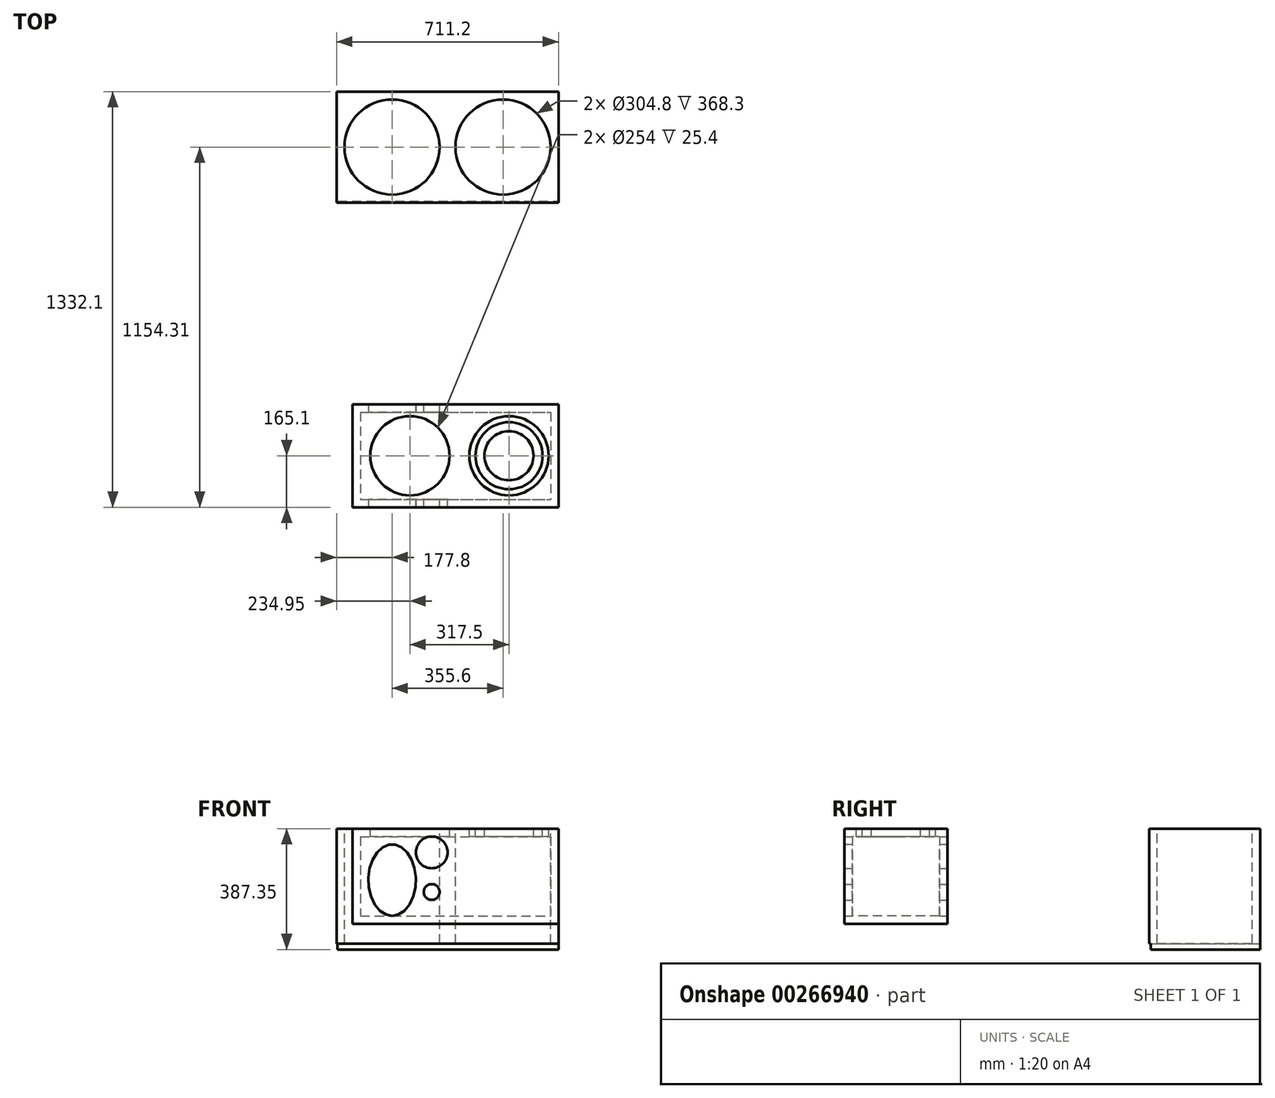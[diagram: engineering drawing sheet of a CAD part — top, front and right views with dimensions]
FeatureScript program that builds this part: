
annotation { "Feature Type Name" : "Feature", "Feature Type Description" : "" }
export const myFeature = defineFeature(function(context is Context, id is Id, definition is map)
    precondition{}
    {
        {
            var Q0;
            Q0=qCreatedBy(makeId("Front.planeOp"),FACE);
            var sketch = newSketch(context, id + "F0", { "sketchPlane" : qUnion([Q0])});
            skLineSegment(sketch, "E0.bottom", {"start": v(-152.4, 304.8) * mm, "end": v(152.4, 304.8) * mm});
            skLineSegment(sketch, "E0.top", {"start": v(-152.4, -304.8) * mm, "end": v(152.4, -304.8) * mm});
            skLineSegment(sketch, "E0.left", {"start": v(-152.4, 304.8) * mm, "end": v(-152.4, -304.8) * mm});
            skLineSegment(sketch, "E0.right", {"start": v(152.4, 304.8) * mm, "end": v(152.4, -304.8) * mm});
            skPoint(sketch, "E1", {"position": v(0, 0) * mm});
            skLineSegment(sketch, "E2", {"start": v(-152.4, 0) * mm, "end": v(152.4, 0) * mm});
            skLineSegment(sketch, "E3", {"start": v(-152.4, 279.4) * mm, "end": v(-127, 279.4) * mm, "construction": true});
            skLineSegment(sketch, "E4", {"start": v(-127, 279.4) * mm, "end": v(-127, 304.8) * mm, "construction": true});
            skLineSegment(sketch, "E5", {"start": v(-127, 304.8) * mm, "end": v(-127, 292.1) * mm, "construction": true});
            skLineSegment(sketch, "E6", {"start": v(-127, 279.4) * mm, "end": v(-127, 0) * mm, "construction": true});
            skLineSegment(sketch, "E7", {"start": v(-127, 279.4) * mm, "end": v(152.4, 279.4) * mm, "construction": true});
            skEllipse(sketch, "E8", {"center": v(-50.8, 165.1) * mm, "majorRadius": 114.3 * mm, "minorRadius": 76.2 * mm, "majorAxis": v(0, 1)});
            skLineSegment(sketch, "E9", {"start": v(152.4, 279.4) * mm, "end": v(127, 279.4) * mm, "construction": true});
            skLineSegment(sketch, "E10", {"start": v(127, 279.4) * mm, "end": v(127, 0) * mm, "construction": true});
            skLineSegment(sketch, "E11", {"start": v(127, 25.4) * mm, "end": v(-127, 25.4) * mm, "construction": true});
            skCircle(sketch, "E12", {"center": v(76.2, 76.2) * mm, "radius": 50.8 * mm});
            skCircle(sketch, "E13", {"center": v(76.2, 203.2) * mm, "radius": 25.4 * mm});
            skLineSegment(sketch, "E14", {"start": v(76.2, 127) * mm, "end": v(76.2, 279.4) * mm, "construction": true});
            skPoint(sketch, "E15", {"position": v(76.2, 127) * mm});
            skLineSegment(sketch, "E16", {"start": v(76.2, 279.4) * mm, "end": v(76.2, 127) * mm, "construction": true});
            skEllipse(sketch, "E17.MirrorC", {"center": v(-50.8, -165.1) * mm, "majorRadius": 114.3 * mm, "minorRadius": 76.2 * mm, "majorAxis": v(0, -1)});
            skCircle(sketch, "E18.MirrorC", {"center": v(76.2, -76.2) * mm, "radius": 50.8 * mm});
            skLineSegment(sketch, "E19.MirrorCS", {"start": v(-152.4, -304.8) * mm, "end": v(-152.4, 304.8) * mm});
            skCircle(sketch, "E20.MirrorC", {"center": v(76.2, -203.2) * mm, "radius": 25.4 * mm});
            skSolve(sketch);
        }
        {
            var Q0;
            {var subQ0=sQuery(id+"F0.wireOp",EDGE,"E0.top");Q0=makeQuery(id+"F0.imprint","IMPRINT",FACE,{"disambiguationData":[TD([[makeQuery(id+"F0.imprint","IMPRINT",EDGE,{"derivedFrom":subQ0}),1.0]])]});}
            extrude(context, id + "F1", {"entities" : qUnion([Q0]), "depth" : 25.4 * mm});
        }
        {
            var Q0;
            Q0=makeQuery(id+"F1.opExtrude","CAP_FACE",FACE,{"disambiguationData":[OSD([sQuery(id+"F0.wireOp",EDGE,"E0.top"),sQuery(id+"F0.wireOp",EDGE,"E0.right"),sQuery(id+"F0.wireOp",EDGE,"E2"),sQuery(id+"F0.wireOp",EDGE,"E17.MirrorC"),sQuery(id+"F0.wireOp",EDGE,"E18.MirrorC"),sQuery(id+"F0.wireOp",EDGE,"E19.MirrorCS"),sQuery(id+"F0.wireOp",EDGE,"E20.MirrorC")])],"isStart":false});
            var sketch = newSketch(context, id + "F2", { "sketchPlane" : qUnion([Q0])});
            skEllipse(sketch, "E21.0", {"center": v(-50.8, -165.1) * mm, "majorRadius": 114.3 * mm, "minorRadius": 76.2 * mm, "majorAxis": v(0, -1)});
            skCircle(sketch, "E22.0", {"center": v(76.2, -76.2) * mm, "radius": 50.8 * mm});
            skCircle(sketch, "E23.0", {"center": v(76.2, -203.2) * mm, "radius": 25.4 * mm});
            skLineSegment(sketch, "E24.0", {"start": v(152.4, 0) * mm, "end": v(152.4, -304.8) * mm});
            skLineSegment(sketch, "E25.0", {"start": v(-152.4, 0) * mm, "end": v(152.4, 0) * mm});
            skLineSegment(sketch, "E26.0", {"start": v(-152.4, -304.8) * mm, "end": v(152.4, -304.8) * mm});
            skLineSegment(sketch, "E27.0", {"start": v(-152.4, -304.8) * mm, "end": v(-152.4, 0) * mm});
            skSolve(sketch);
        }
        {
            var Q0;
            Q0=makeQuery(id+"F2.imprint","IMPRINT",FACE,{"disambiguationData":[TD([[makeQuery(id+"F2.imprint","IMPRINT",EDGE,{"derivedFrom":sQuery(id+"F2.wireOp",EDGE,"E21.0")}),-1.0]])]});
            extrude(context, id + "F3", {"entities" : qUnion([Q0]), "operationType" : NewBodyOperationType.ADD, "depth" : 304.8 * mm});
        }
        {
            var Q0;
            Q0=makeQuery(id+"F3.boolean.opBoolean","MERGE",FACE,{"derivedFrom":[makeQuery(id+"F1.opExtrude","SWEPT_FACE",FACE,{"disambiguationData":[OSD([sQuery(id+"F0.wireOp",EDGE,"E2")])]}),makeQuery(id+"F3.opExtrude","SWEPT_FACE",FACE,{"disambiguationData":[OSD([sQuery(id+"F2.wireOp",EDGE,"E25.0")])]})]});
            var sketch = newSketch(context, id + "F4", { "sketchPlane" : qUnion([Q0])});
            skLineSegment(sketch, "E28.bottom", {"start": v(-126.23, -299.99) * mm, "end": v(123.64, -299.99) * mm});
            skLineSegment(sketch, "E28.top", {"start": v(-126.23, -26.64) * mm, "end": v(123.64, -26.64) * mm});
            skLineSegment(sketch, "E28.left", {"start": v(-126.23, -299.99) * mm, "end": v(-126.23, -26.64) * mm});
            skLineSegment(sketch, "E28.right", {"start": v(123.64, -299.99) * mm, "end": v(123.64, -26.64) * mm});
            skSolve(sketch);
        }
        {
            var Q0;
            Q0=makeQuery(id+"F3.boolean.opBoolean","MERGE",FACE,{"derivedFrom":[makeQuery(id+"F1.opExtrude","SWEPT_FACE",FACE,{"disambiguationData":[OSD([sQuery(id+"F0.wireOp",EDGE,"E0.right")])]}),makeQuery(id+"F3.opExtrude","SWEPT_FACE",FACE,{"disambiguationData":[OSD([sQuery(id+"F2.wireOp",EDGE,"E24.0")])]})]});
            var sketch = newSketch(context, id + "F5", { "sketchPlane" : qUnion([Q0])});
            skLineSegment(sketch, "E29.bottom", {"start": v(-25.4, -25.4) * mm, "end": v(-304.8, -25.4) * mm});
            skLineSegment(sketch, "E29.top", {"start": v(-25.4, -279.4) * mm, "end": v(-304.8, -279.4) * mm});
            skLineSegment(sketch, "E29.left", {"start": v(-25.4, -25.4) * mm, "end": v(-25.4, -279.4) * mm});
            skLineSegment(sketch, "E29.right", {"start": v(-304.8, -25.4) * mm, "end": v(-304.8, -279.4) * mm});
            skSolve(sketch);
        }
        {
            var Q0;
            Q0=makeQuery(id+"F5.imprint","IMPRINT",FACE,{"disambiguationData":[TD([[makeQuery(id+"F5.imprint","IMPRINT",EDGE,{"derivedFrom":sQuery(id+"F5.wireOp",EDGE,"E29.bottom")}),1.0]])]});
            extrude(context, id + "F18", {"entities" : qUnion([Q0]), "operationType" : NewBodyOperationType.REMOVE, "endBound" : BoundingType.THROUGH_ALL, "oppositeDirection" : true, "depth" : 25.4 * mm});
        }
        {
            var Q0;
            Q0=makeQuery(id+"F3.boolean.opBoolean","MERGE",FACE,{"derivedFrom":[makeQuery(id+"F1.opExtrude","SWEPT_FACE",FACE,{"disambiguationData":[OSD([sQuery(id+"F0.wireOp",EDGE,"E0.right")])]}),makeQuery(id+"F3.opExtrude","SWEPT_FACE",FACE,{"disambiguationData":[OSD([sQuery(id+"F2.wireOp",EDGE,"E24.0")])]})]});
            extrude(context, id + "F19", {"entities" : qUnion([Q0]), "operationType" : NewBodyOperationType.ADD, "depth" : 304.8 * mm});
        }
        {
            var Q0;
            Q0=makeQuery(id+"F19.opExtrude","CAP_FACE",FACE,{"disambiguationData":[OSD([sQuery(id+"F0.wireOp",EDGE,"E0.right"),sQuery(id+"F2.wireOp",EDGE,"E24.0")])],"isStart":false});
            var sketch = newSketch(context, id + "F6", { "sketchPlane" : qUnion([Q0])});
            skLineSegment(sketch, "E30.bottom", {"start": v(0, -304.8) * mm, "end": v(-330.2, -304.8) * mm});
            skLineSegment(sketch, "E30.top", {"start": v(0, 0) * mm, "end": v(-330.2, 0) * mm});
            skLineSegment(sketch, "E30.left", {"start": v(0, -304.8) * mm, "end": v(0, 0) * mm});
            skLineSegment(sketch, "E30.right", {"start": v(-330.2, -304.8) * mm, "end": v(-330.2, 0) * mm});
            skSolve(sketch);
        }
        {
            var Q0;
            Q0 = qSketchRegion(id + "F6", true);
            extrude(context, id + "F7", {"entities" : qUnion([Q0]), "operationType" : NewBodyOperationType.ADD, "depth" : 25.4 * mm});
        }
        {
            var Q0;
            {var subQ0=sQuery(id+"F2.wireOp",EDGE,"E25.0");var subQ1=sQuery(id+"F0.wireOp",EDGE,"E2");Q0=makeQuery(id+"F7.boolean.opBoolean","MERGE",FACE,{"derivedFrom":[makeQuery(id+"F19.boolean.opBoolean","MERGE",FACE,{"derivedFrom":[makeQuery(id+"F3.boolean.opBoolean","MERGE",FACE,{"derivedFrom":[makeQuery(id+"F1.opExtrude","SWEPT_FACE",FACE,{"disambiguationData":[OSD([subQ1])]}),makeQuery(id+"F3.opExtrude","SWEPT_FACE",FACE,{"disambiguationData":[OSD([subQ0])]})]}),makeQuery(id+"F19.opExtrude","SWEPT_FACE",FACE,{"disambiguationData":[OSD([sQuery(id+"F0.wireOp",EDGE,"E0.right"),subQ1,sQuery(id+"F2.wireOp",EDGE,"E24.0"),subQ0])]})]}),makeQuery(id+"F7.opExtrude","SWEPT_FACE",FACE,{"disambiguationData":[OSD([sQuery(id+"F6.wireOp",EDGE,"E30.top")])]})]});}
            var sketch = newSketch(context, id + "F20", { "sketchPlane" : qUnion([Q0])});
            skLineSegment(sketch, "E31.bottom", {"start": v(482.6, -330.2) * mm, "end": v(165.1, -330.2) * mm});
            skLineSegment(sketch, "E31.top", {"start": v(482.6, 0) * mm, "end": v(165.1, 0) * mm});
            skLineSegment(sketch, "E31.left", {"start": v(482.6, -330.2) * mm, "end": v(482.6, 0) * mm});
            skLineSegment(sketch, "E32.bottom", {"start": v(-152.4, 0) * mm, "end": v(165.1, 0) * mm});
            skLineSegment(sketch, "E32.top", {"start": v(-152.4, -330.2) * mm, "end": v(165.1, -330.2) * mm});
            skLineSegment(sketch, "E32.left", {"start": v(-152.4, 0) * mm, "end": v(-152.4, -330.2) * mm});
            skPoint(sketch, "E33", {"position": v(6.35, -165.1) * mm});
            skCircle(sketch, "E34", {"center": v(6.35, -165.1) * mm, "radius": 127 * mm});
            skPoint(sketch, "E35", {"position": v(323.85, -165.1) * mm});
            skCircle(sketch, "E36", {"center": v(323.85, -165.1) * mm, "radius": 127 * mm});
            skSolve(sketch);
        }
        {
            var Q0;
            Q0=makeQuery(id+"F20.imprint","IMPRINT",FACE,{"disambiguationData":[TD([[makeQuery(id+"F20.imprint","IMPRINT",EDGE,{"derivedFrom":sQuery(id+"F20.wireOp",EDGE,"E36")}),1.0]])]});
            var Q1;
            Q1=makeQuery(id+"F20.imprint","IMPRINT",FACE,{"disambiguationData":[TD([[makeQuery(id+"F20.imprint","IMPRINT",EDGE,{"derivedFrom":sQuery(id+"F20.wireOp",EDGE,"E34")}),1.0]])]});
            extrude(context, id + "F21", {"entities" : qUnion([Q0, Q1]), "operationType" : NewBodyOperationType.REMOVE, "endBound" : BoundingType.UP_TO_NEXT, "oppositeDirection" : true, "depth" : 25.4 * mm});
        }
        {
            var Q0;
            {var subQ0=sQuery(id+"F2.wireOp",EDGE,"E25.0");var subQ1=sQuery(id+"F0.wireOp",EDGE,"E2");Q0=makeQuery(id+"F7.boolean.opBoolean","MERGE",FACE,{"derivedFrom":[makeQuery(id+"F19.boolean.opBoolean","MERGE",FACE,{"derivedFrom":[makeQuery(id+"F3.boolean.opBoolean","MERGE",FACE,{"derivedFrom":[makeQuery(id+"F1.opExtrude","SWEPT_FACE",FACE,{"disambiguationData":[OSD([subQ1])]}),makeQuery(id+"F3.opExtrude","SWEPT_FACE",FACE,{"disambiguationData":[OSD([subQ0])]})]}),makeQuery(id+"F19.opExtrude","SWEPT_FACE",FACE,{"disambiguationData":[OSD([sQuery(id+"F0.wireOp",EDGE,"E0.right"),subQ1,sQuery(id+"F2.wireOp",EDGE,"E24.0"),subQ0])]})]}),makeQuery(id+"F7.opExtrude","SWEPT_FACE",FACE,{"disambiguationData":[OSD([sQuery(id+"F6.wireOp",EDGE,"E30.top")])]})]});}
            var sketch = newSketch(context, id + "F8", { "sketchPlane" : qUnion([Q0])});
            skCircle(sketch, "E37", {"center": v(323.85, -165.1) * mm, "radius": 107.46 * mm});
            skCircle(sketch, "E38", {"center": v(323.85, -165.1) * mm, "radius": 78.61 * mm});
            skSolve(sketch);
        }
        {
            var Q0;
            Q0=makeQuery(id+"F8.imprint","IMPRINT",FACE,{"disambiguationData":[TD([[makeQuery(id+"F8.imprint","IMPRINT",EDGE,{"derivedFrom":sQuery(id+"F8.wireOp",EDGE,"E37")}),1.0]])]});
            extrude(context, id + "F9", {"entities" : qUnion([Q0]), "oppositeDirection" : true, "depth" : 25.4 * mm});
        }
        {
            var Q0;
            Q0=makeQuery(id+"F3.boolean.opBoolean","MERGE",FACE,{"derivedFrom":[makeQuery(id+"F1.opExtrude","SWEPT_FACE",FACE,{"disambiguationData":[OSD([sQuery(id+"F0.wireOp",EDGE,"E19.MirrorCS")])]}),makeQuery(id+"F3.opExtrude","SWEPT_FACE",FACE,{"disambiguationData":[OSD([sQuery(id+"F2.wireOp",EDGE,"E27.0")])]})]});
            var sketch = newSketch(context, id + "F10", { "sketchPlane" : qUnion([Q0])});
            skLineSegment(sketch, "E39.bottom", {"start": v(330.2, -304.8) * mm, "end": v(0, -304.8) * mm});
            skLineSegment(sketch, "E39.top", {"start": v(330.2, 0) * mm, "end": v(0, 0) * mm});
            skLineSegment(sketch, "E39.left", {"start": v(330.2, -304.8) * mm, "end": v(330.2, 0) * mm});
            skLineSegment(sketch, "E39.right", {"start": v(0, -304.8) * mm, "end": v(0, 0) * mm});
            skSolve(sketch);
        }
        {
            var Q0;
            Q0 = qSketchRegion(id + "F10", true);
            extrude(context, id + "F11", {"entities" : qUnion([Q0]), "operationType" : NewBodyOperationType.ADD, "depth" : 25.4 * mm});
        }
        {
            var Q0;
            {var subQ0=sQuery(id+"F2.wireOp",EDGE,"E25.0");var subQ1=sQuery(id+"F0.wireOp",EDGE,"E2");Q0=makeQuery(id+"F11.boolean.opBoolean","MERGE",FACE,{"derivedFrom":[makeQuery(id+"F7.boolean.opBoolean","MERGE",FACE,{"derivedFrom":[makeQuery(id+"F19.boolean.opBoolean","MERGE",FACE,{"derivedFrom":[makeQuery(id+"F3.boolean.opBoolean","MERGE",FACE,{"derivedFrom":[makeQuery(id+"F1.opExtrude","SWEPT_FACE",FACE,{"disambiguationData":[OSD([subQ1])]}),makeQuery(id+"F3.opExtrude","SWEPT_FACE",FACE,{"disambiguationData":[OSD([subQ0])]})]}),makeQuery(id+"F19.opExtrude","SWEPT_FACE",FACE,{"disambiguationData":[OSD([sQuery(id+"F0.wireOp",EDGE,"E0.right"),subQ1,sQuery(id+"F2.wireOp",EDGE,"E24.0"),subQ0])]})]}),makeQuery(id+"F7.opExtrude","SWEPT_FACE",FACE,{"disambiguationData":[OSD([sQuery(id+"F6.wireOp",EDGE,"E30.top")])]})]}),makeQuery(id+"F11.opExtrude","SWEPT_FACE",FACE,{"disambiguationData":[OSD([sQuery(id+"F10.wireOp",EDGE,"E39.top")])]})]});}
            var sketch = newSketch(context, id + "F12", { "sketchPlane" : qUnion([Q0])});
            skLineSegment(sketch, "E40", {"start": v(482.6, 0) * mm, "end": v(482.6, 646.3) * mm});
            skLineSegment(sketch, "E41.bottom", {"start": v(482.6, 646.3) * mm, "end": v(-228.6, 646.3) * mm});
            skLineSegment(sketch, "E41.top", {"start": v(482.6, 1001.9) * mm, "end": v(-228.6, 1001.9) * mm});
            skLineSegment(sketch, "E41.left", {"start": v(482.6, 646.3) * mm, "end": v(482.6, 1001.9) * mm});
            skLineSegment(sketch, "E41.right", {"start": v(-228.6, 646.3) * mm, "end": v(-228.6, 1001.9) * mm});
            skLineSegment(sketch, "E42", {"start": v(127, 1001.9) * mm, "end": v(127, 646.3) * mm, "construction": true});
            skLineSegment(sketch, "E43", {"start": v(-228.6, 824.1) * mm, "end": v(127, 824.1) * mm, "construction": true});
            skLineSegment(sketch, "E44", {"start": v(127, 824.1) * mm, "end": v(482.6, 824.1) * mm, "construction": true});
            skCircle(sketch, "E45", {"center": v(-50.8, 824.1) * mm, "radius": 152.4 * mm});
            skCircle(sketch, "E46", {"center": v(304.8, 824.1) * mm, "radius": 152.4 * mm});
            skSolve(sketch);
        }
        {
            var Q0;
            Q0 = qSketchRegion(id + "F12", true);
            extrude(context, id + "F13", {"entities" : qUnion([Q0]), "oppositeDirection" : true, "depth" : 19.05 * mm});
        }
        {
            var Q0;
            Q0=makeQuery(id+"F13.opExtrude","CAP_FACE",FACE,{"disambiguationData":[OSD([sQuery(id+"F12.wireOp",EDGE,"E41.bottom"),sQuery(id+"F12.wireOp",EDGE,"E41.top"),sQuery(id+"F12.wireOp",EDGE,"E41.left"),sQuery(id+"F12.wireOp",EDGE,"E41.right"),sQuery(id+"F12.wireOp",EDGE,"E45"),sQuery(id+"F12.wireOp",EDGE,"E46")])],"isStart":false});
            var sketch = newSketch(context, id + "F14", { "sketchPlane" : qUnion([Q0])});
            skLineSegment(sketch, "E47", {"start": v(127, -1001.9) * mm, "end": v(133.35, -1001.9) * mm});
            skLineSegment(sketch, "E48", {"start": v(133.35, -1001.9) * mm, "end": v(133.35, -646.3) * mm});
            skLineSegment(sketch, "E49", {"start": v(127, -1001.9) * mm, "end": v(120.65, -1001.9) * mm});
            skLineSegment(sketch, "E50", {"start": v(120.65, -1001.9) * mm, "end": v(120.65, -646.3) * mm});
            skPoint(sketch, "E51.start.orphan", {"position": v(127, -646.3) * mm});
            skSolve(sketch);
        }
        {
            var Q0;
            Q0 = qSketchRegion(id + "F14", true);
            var Q1;
            Q1=makeQuery(id+"F14.imprint","IMPRINT",FACE,{"disambiguationData":[TD([[makeQuery(id+"F14.imprint","IMPRINT",EDGE,{"derivedFrom":sQuery(id+"F14.wireOp",EDGE,"E47")}),-1.0]])]});
            extrude(context, id + "F15", {"entities" : qUnion([Q0, Q1]), "operationType" : NewBodyOperationType.ADD, "depth" : 317.5 * mm});
        }
        {
            var Q0;
            {var subQ0=sQuery(id+"F12.wireOp",EDGE,"E45");var subQ1=sQuery(id+"F12.wireOp",EDGE,"E41.top");var subQ2=sQuery(id+"F12.wireOp",EDGE,"E41.right");var subQ3=sQuery(id+"F12.wireOp",EDGE,"E41.bottom");Q0=makeQuery(id+"F15.boolean.opBoolean","SPLIT",FACE,{"disambiguationData":[TD([makeQuery(id+"F13.opExtrude","SWEPT_FACE",FACE,{"disambiguationData":[OSD([subQ2])]})])],"derivedFrom":makeQuery(id+"F13.opExtrude","CAP_FACE",FACE,{"disambiguationData":[OSD([subQ3,subQ1,sQuery(id+"F12.wireOp",EDGE,"E41.left"),subQ2,subQ0,sQuery(id+"F12.wireOp",EDGE,"E46")])],"isStart":false})});}
            var Q1;
            {var subQ0=sQuery(id+"F12.wireOp",EDGE,"E46");var subQ1=sQuery(id+"F12.wireOp",EDGE,"E41.bottom");var subQ2=sQuery(id+"F12.wireOp",EDGE,"E41.top");var subQ3=sQuery(id+"F12.wireOp",EDGE,"E41.left");Q1=makeQuery(id+"F15.boolean.opBoolean","SPLIT",FACE,{"disambiguationData":[TD([makeQuery(id+"F13.opExtrude","SWEPT_FACE",FACE,{"disambiguationData":[OSD([subQ3])]})])],"derivedFrom":makeQuery(id+"F13.opExtrude","CAP_FACE",FACE,{"disambiguationData":[OSD([subQ1,subQ2,subQ3,sQuery(id+"F12.wireOp",EDGE,"E41.right"),sQuery(id+"F12.wireOp",EDGE,"E45"),subQ0])],"isStart":false})});}
            extrude(context, id + "F22", {"entities" : qUnion([Q0, Q1]), "operationType" : NewBodyOperationType.ADD, "depth" : 349.25 * mm});
        }
        {
            var Q0;
            Q0=makeQuery(id+"F15.opExtrude","CAP_FACE",FACE,{"disambiguationData":[OSD([sQuery(id+"F12.wireOp",EDGE,"E41.bottom"),sQuery(id+"F14.wireOp",EDGE,"E47"),sQuery(id+"F14.wireOp",EDGE,"E48"),sQuery(id+"F14.wireOp",EDGE,"E49"),sQuery(id+"F14.wireOp",EDGE,"E50")])],"isStart":false});
            extrude(context, id + "F16", {"entities" : qUnion([Q0]), "operationType" : NewBodyOperationType.ADD, "depth" : 31.75 * mm});
        }
        {
            var Q0;
            {var subQ0=sQuery(id+"F14.wireOp",EDGE,"E50");var subQ1=sQuery(id+"F14.wireOp",EDGE,"E49");var subQ2=sQuery(id+"F14.wireOp",EDGE,"E48");var subQ3=sQuery(id+"F14.wireOp",EDGE,"E47");var subQ4=sQuery(id+"F12.wireOp",EDGE,"E41.bottom");var subQ5=sQuery(id+"F12.wireOp",EDGE,"E45");var subQ6=sQuery(id+"F12.wireOp",EDGE,"E41.top");var subQ8=sQuery(id+"F12.wireOp",EDGE,"E41.right");var subQ12=sQuery(id+"F12.wireOp",EDGE,"E46");var subQ13=sQuery(id+"F12.wireOp",EDGE,"E41.left");var subQ14=makeQuery(id+"F13.opExtrude","CAP_FACE",FACE,{"disambiguationData":[OSD([subQ4,subQ6,subQ13,subQ8,subQ5,subQ12])],"isStart":false});Q0=makeQuery(id+"F16.boolean.opBoolean","MERGE",FACE,{"derivedFrom":[makeQuery(id+"F22.opExtrude","CAP_FACE",FACE,{"disambiguationData":[OSD([subQ4,subQ6,subQ13,subQ8,subQ5,subQ12]),TDD([makeQuery(id+"F15.boolean.opBoolean","SPLIT",FACE,{"disambiguationData":[TD([makeQuery(id+"F13.opExtrude","SWEPT_FACE",FACE,{"disambiguationData":[OSD([subQ13])]})])],"derivedFrom":subQ14})])],"isStart":false}),makeQuery(id+"F22.opExtrude","CAP_FACE",FACE,{"disambiguationData":[OSD([subQ4,subQ6,subQ13,subQ8,subQ5,subQ12]),TDD([makeQuery(id+"F15.boolean.opBoolean","SPLIT",FACE,{"disambiguationData":[TD([makeQuery(id+"F13.opExtrude","SWEPT_FACE",FACE,{"disambiguationData":[OSD([subQ8])]})])],"derivedFrom":subQ14})])],"isStart":false}),makeQuery(id+"F16.opExtrude","CAP_FACE",FACE,{"disambiguationData":[OSD([subQ4,subQ3,subQ2,subQ1,subQ0])],"isStart":false})]});}
            var sketch = newSketch(context, id + "F23", { "sketchPlane" : qUnion([Q0])});
            skLineSegment(sketch, "E52.bottom", {"start": v(-225.24, -651) * mm, "end": v(482.6, -651) * mm});
            skLineSegment(sketch, "E52.top", {"start": v(-225.24, -1001.9) * mm, "end": v(482.6, -1001.9) * mm});
            skLineSegment(sketch, "E52.left", {"start": v(-225.24, -651) * mm, "end": v(-225.24, -1001.9) * mm});
            skLineSegment(sketch, "E52.right", {"start": v(482.6, -651) * mm, "end": v(482.6, -1001.9) * mm});
            skSolve(sketch);
        }
        {
            var Q0;
            Q0 = qSketchRegion(id + "F23", true);
            extrude(context, id + "F17", {"entities" : qUnion([Q0]), "operationType" : NewBodyOperationType.ADD, "depth" : 19.05 * mm});
        }
    });
